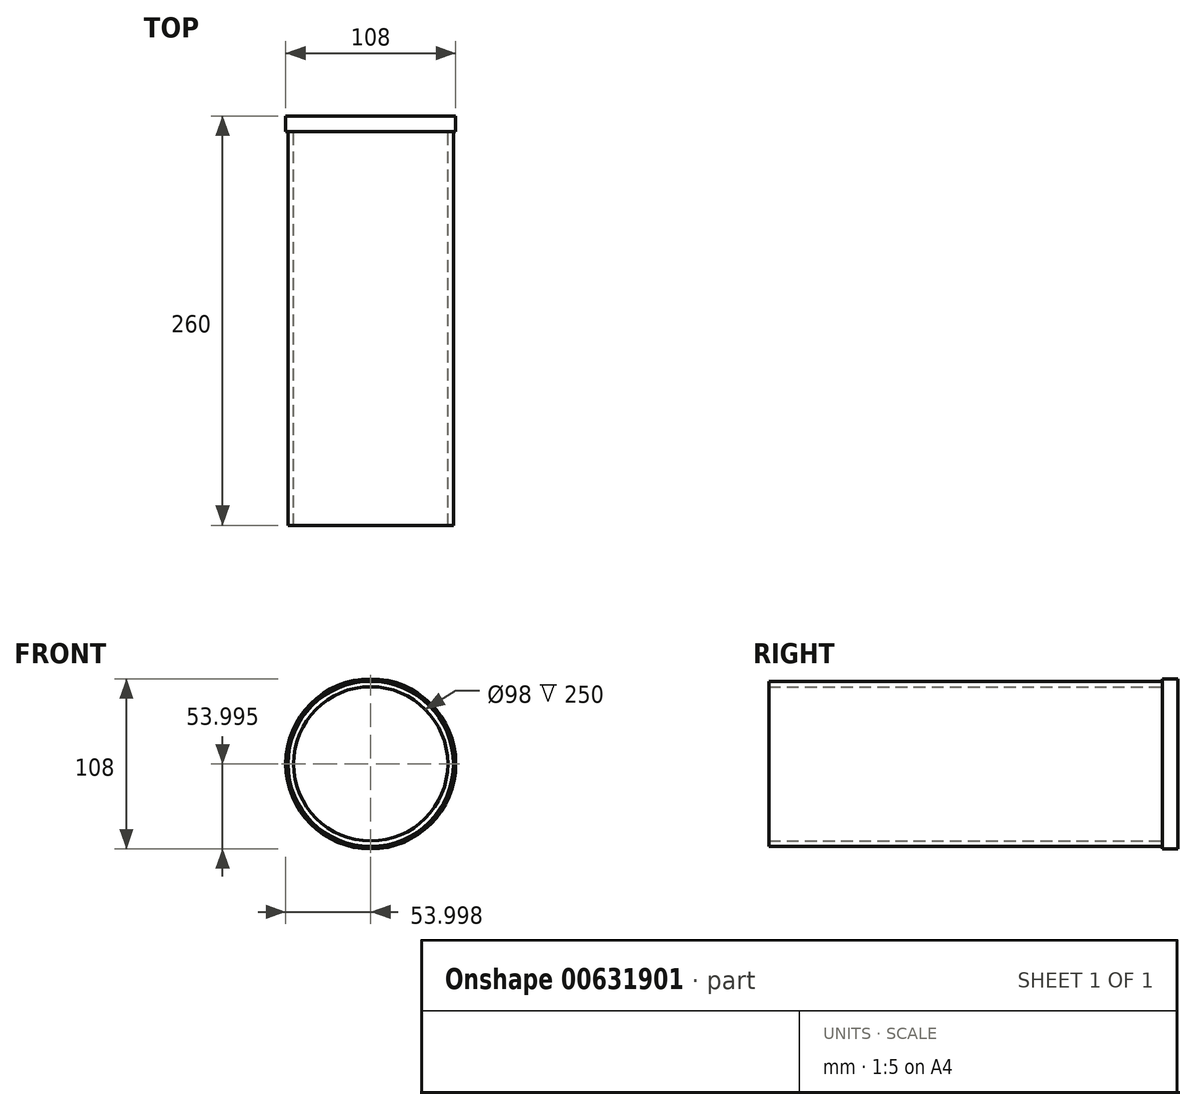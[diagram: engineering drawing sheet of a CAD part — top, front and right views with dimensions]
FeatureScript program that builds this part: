
annotation { "Feature Type Name" : "Feature", "Feature Type Description" : "" }
export const myFeature = defineFeature(function(context is Context, id is Id, definition is map)
    precondition{}
    {
        {
            var Q0;
            Q0=qCreatedBy(makeId("Front.planeOp"),FACE);
            var sketch = newSketch(context, id + "F0", { "sketchPlane" : qUnion([Q0])});
            skCircle(sketch, "E0", {"center": v(-34.7, 40.83) * mm, "radius": 49 * mm});
            skCircle(sketch, "E1", {"center": v(-34.7, 40.83) * mm, "radius": 52.5 * mm});
            skSolve(sketch);
        }
        {
            var Q0;
            Q0=makeQuery(id+"F0.imprint","IMPRINT",FACE,{"disambiguationData":[TD([[makeQuery(id+"F0.imprint","IMPRINT",EDGE,{"derivedFrom":sQuery(id+"F0.wireOp",EDGE,"E0")}),-1.0]])]});
            extrude(context, id + "F1", {"entities" : qUnion([Q0]), "depth" : 250 * mm, "offsetDistance" : 25 * mm});
        }
        {
            var Q0;
            Q0=makeQuery(id+"F1.opExtrude","CAP_FACE",FACE,{"disambiguationData":[OSD([sQuery(id+"F0.wireOp",EDGE,"E0"),sQuery(id+"F0.wireOp",EDGE,"E1")])],"isStart":true});
            var sketch = newSketch(context, id + "F2", { "sketchPlane" : qUnion([Q0])});
            skCircle(sketch, "E2", {"center": v(34.7, 40.83) * mm, "radius": 54 * mm});
            skSolve(sketch);
        }
        {
            var Q0;
            Q0 = qSketchRegion(id + "F2", true);
            extrude(context, id + "F3", {"entities" : qUnion([Q0]), "operationType" : NewBodyOperationType.ADD, "depth" : 10 * mm, "offsetDistance" : 25 * mm});
        }
    });
